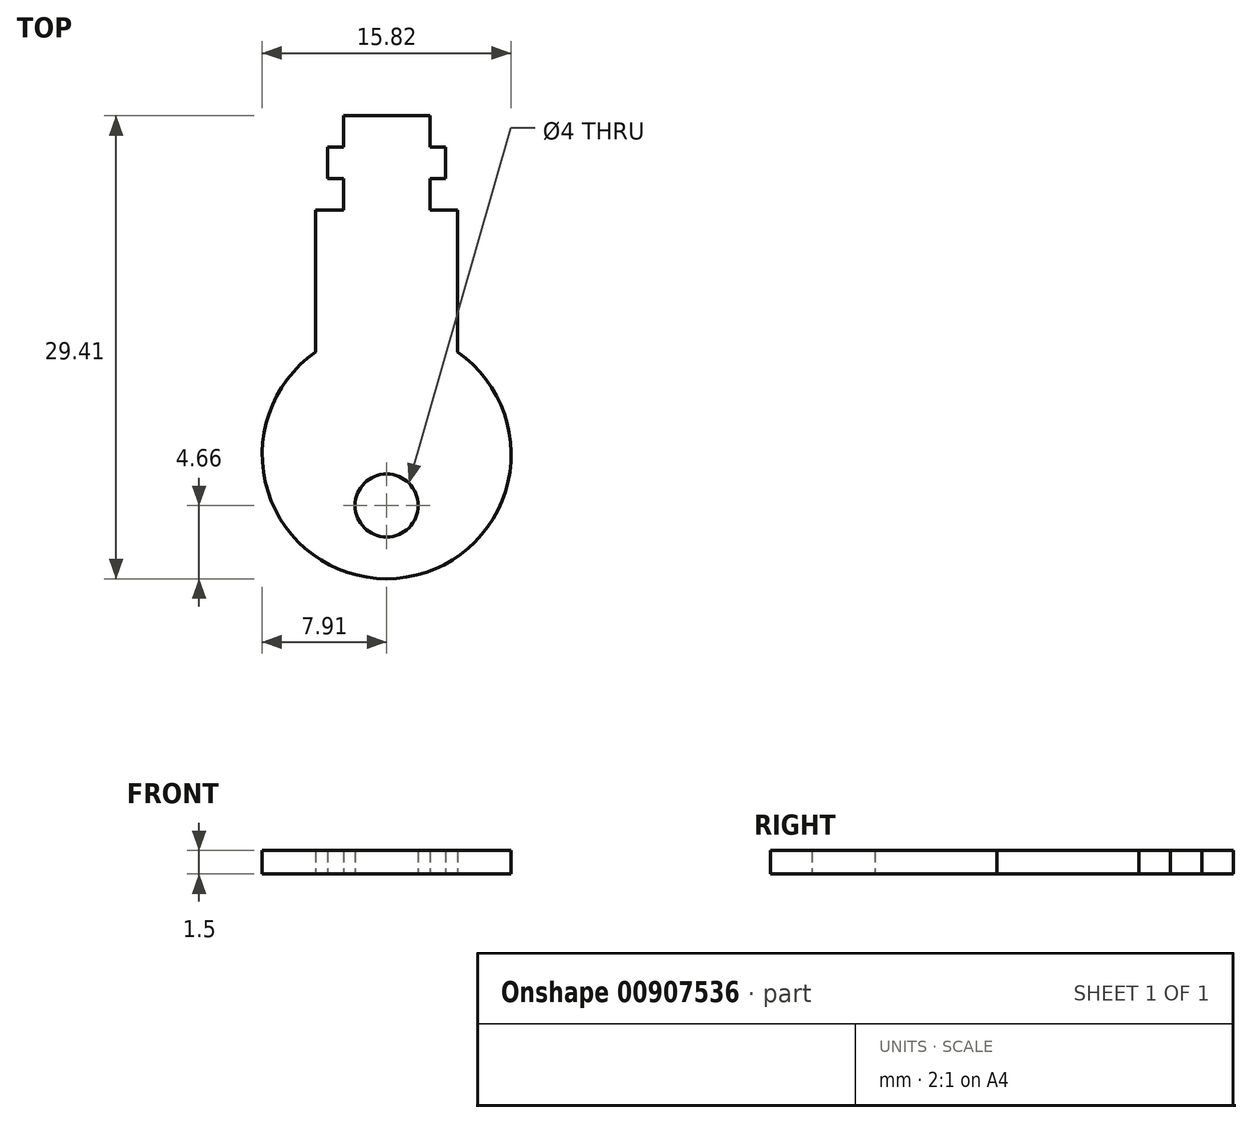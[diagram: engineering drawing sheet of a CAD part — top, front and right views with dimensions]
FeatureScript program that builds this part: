
annotation { "Feature Type Name" : "Feature", "Feature Type Description" : "" }
export const myFeature = defineFeature(function(context is Context, id is Id, definition is map)
    precondition{}
    {
        {
            var Q0;
            Q0=qCreatedBy(makeId("Top.planeOp"),FACE);
            var sketch = newSketch(context, id + "F0", { "sketchPlane" : qUnion([Q0])});
            skLineSegment(sketch, "E0.bottom", {"start": v(4.5, 4.5) * mm, "end": v(2.75, 4.5) * mm});
            skLineSegment(sketch, "E0.left", {"start": v(4.5, 4.5) * mm, "end": v(4.5, -4.5) * mm});
            skLineSegment(sketch, "E0.right", {"start": v(-4.5, 4.5) * mm, "end": v(-4.5, -4.5) * mm});
            skPoint(sketch, "E0.middle", {"position": v(0, 0) * mm});
            skLineSegment(sketch, "E1", {"start": v(-2.75, 4.5) * mm, "end": v(-2.75, 6.5) * mm});
            skLineSegment(sketch, "E2.MirrorCS", {"start": v(2.75, 4.5) * mm, "end": v(2.75, 6.5) * mm});
            skLineSegment(sketch, "E3", {"start": v(-2.75, 10.5) * mm, "end": v(2.75, 10.5) * mm});
            skLineSegment(sketch, "E4", {"start": v(-2.75, 4.5) * mm, "end": v(-2.75, 6.5) * mm, "construction": true});
            skLineSegment(sketch, "E5", {"start": v(-2.75, 6.5) * mm, "end": v(-3.75, 6.5) * mm, "construction": true});
            skLineSegment(sketch, "E6", {"start": v(-3.75, 6.5) * mm, "end": v(-3.75, 8.5) * mm});
            skLineSegment(sketch, "E7", {"start": v(-3.75, 8.5) * mm, "end": v(-2.75, 8.5) * mm});
            skLineSegment(sketch, "E8.MirrorCS", {"start": v(3.75, 8.5) * mm, "end": v(2.75, 8.5) * mm});
            skLineSegment(sketch, "E9.MirrorCS", {"start": v(3.75, 6.5) * mm, "end": v(3.75, 8.5) * mm});
            skLineSegment(sketch, "E10.MirrorCS", {"start": v(2.75, 6.5) * mm, "end": v(3.75, 6.5) * mm, "construction": true});
            skLineSegment(sketch, "E11", {"start": v(2.75, 6.5) * mm, "end": v(3.75, 6.5) * mm});
            skLineSegment(sketch, "E12", {"start": v(-3.75, 6.5) * mm, "end": v(-2.75, 6.5) * mm});
            skLineSegment(sketch, "E13", {"start": v(7.9, -11) * mm, "end": v(8.5, -11) * mm});
            skLineSegment(sketch, "E14.MirrorCS", {"start": v(-7.9, -11) * mm, "end": v(-8.5, -11) * mm});
            skArc(sketch, "E15", {"start": v(-4.5, -4.5) * mm, "mid": v(0, -18.9) * mm, "end": v(4.5, -4.5) * mm});
            skPoint(sketch, "E16.orphan", {"position": v(0, -4.5) * mm});
            skPoint(sketch, "E17.end.orphan", {"position": v(0, -17.5) * mm});
            skLineSegment(sketch, "E18", {"start": v(0, -11) * mm, "end": v(0, -17.5) * mm});
            skCircle(sketch, "E19", {"center": v(0, -14.25) * mm, "radius": 2 * mm});
            skLineSegment(sketch, "E20.trimOffspring", {"start": v(-2.75, 8.5) * mm, "end": v(-2.75, 10.5) * mm});
            skPoint(sketch, "E21.MirrorCS.start.orphan", {"position": v(0, 4.5) * mm});
            skLineSegment(sketch, "E22.trimOffspring", {"start": v(-2.75, 4.5) * mm, "end": v(-4.5, 4.5) * mm});
            skLineSegment(sketch, "E23.trimOffspring", {"start": v(2.75, 8.5) * mm, "end": v(2.75, 10.5) * mm});
            skPoint(sketch, "E24.end.orphan", {"position": v(2.75, 4.5) * mm});
            skSolve(sketch);
        }
        {
            var Q0;
            Q0=makeQuery(id+"F0.imprint","IMPRINT",FACE,{"disambiguationData":[TD([[makeQuery(id+"F0.imprint","IMPRINT",EDGE,{"derivedFrom":sQuery(id+"F0.wireOp",EDGE,"E0.bottom")}),1.0]])]});
            extrude(context, id + "F1", {"entities" : qUnion([Q0]), "depth" : 1.5 * mm, "offsetDistance" : 25 * mm});
        }
    });
